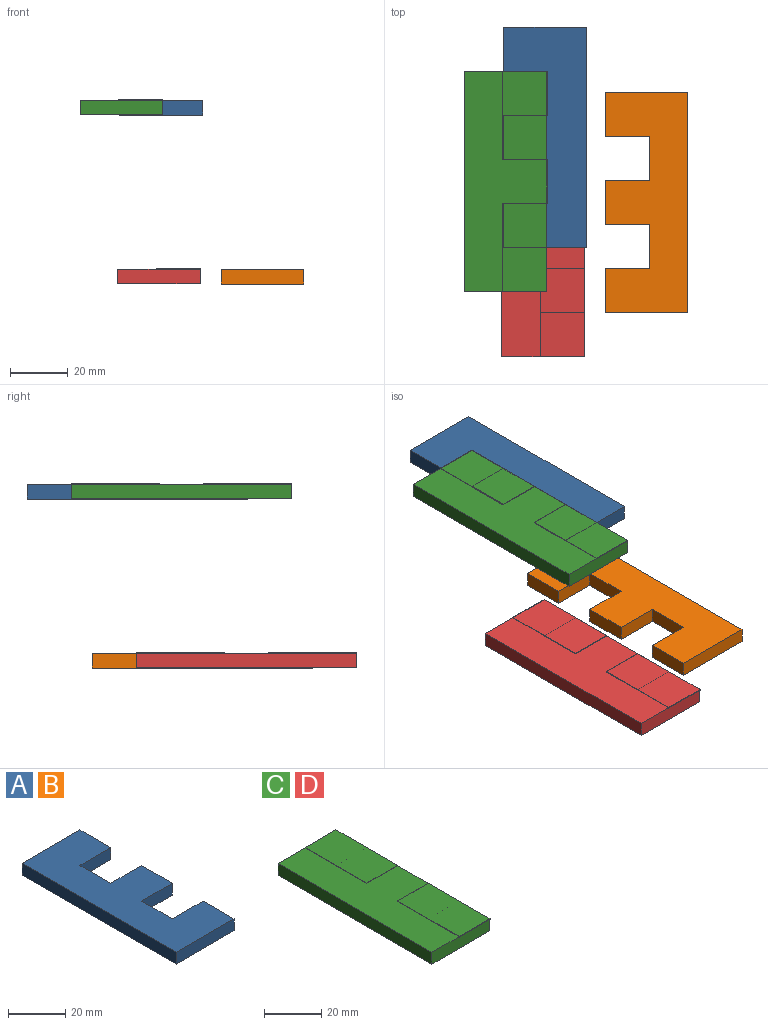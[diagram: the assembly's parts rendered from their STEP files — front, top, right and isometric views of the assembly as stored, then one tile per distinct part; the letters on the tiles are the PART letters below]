
ASSEMBLY  parts=4 mates=2
PART A: 14 faces, bbox 28.6x76.2x5.1 mm
  f0: plane 76.2x5.08mm, normal (-1,0,0), area 387.1mm2, adj f1,f11,f12,f13
  f1: plane 28.64x5.08mm, normal (0,-1,0), area 145.5mm2, adj f0,f2,f12,f13
  f2: plane 15.24x5.08mm, normal (1,0,0), area 77.4mm2, adj f1,f3,f12,f13
  f3: plane 15.24x5.08mm, normal (0,1,0), area 77.4mm2, adj f2,f4,f12,f13
  f4: plane 15.24x5.08mm, normal (1,0,0), area 77.4mm2, adj f3,f5,f12,f13
  f5: plane 15.24x5.08mm, normal (0,-1,0), area 77.4mm2, adj f4,f6,f12,f13
  f6: plane 15.24x5.08mm, normal (1,0,0), area 77.4mm2, adj f5,f7,f12,f13
  f7: plane 15.24x5.08mm, normal (0,1,0), area 77.4mm2, adj f6,f8,f12,f13
  f8: plane 15.24x5.08mm, normal (1,0,0), area 77.4mm2, adj f7,f9,f12,f13
  f9: plane 15.24x5.08mm, normal (0,-1,0), area 77.4mm2, adj f8,f10,f12,f13
  f10: plane 15.24x5.08mm, normal (1,0,0), area 77.4mm2, adj f9,f11,f12,f13
  f11: plane 28.64x5.08mm, normal (0,1,0), area 145.5mm2, adj f0,f10,f12,f13
  f12: plane 76.2x28.64mm, normal (0,0,1), area 1718.2mm2, adj f0,f1,f2,f3,f4,f5,f6,f7
  f13: plane 76.2x28.64mm, normal (0,0,-1), area 1718.2mm2, adj f0,f1,f2,f3,f4,f5,f6,f7
PART B: same geometry as A
PART C: 24 faces, bbox 28.6x76.3x5.2 mm
  f0: plane 15.24x5.08mm, normal (1,0,0), area 75.5mm2, adj f1,f7,f11,f12,f18,f20
  f1: plane 15.24x4.95mm, normal (0,1,0), area 75.5mm2, adj f0,f6,f11,f18
  f2: plane 15.24x4.95mm, normal (0,1,0), area 75.5mm2, adj f8,f9,f11,f13
  f3: plane 15.24x4.95mm, normal (0,-1,0), area 75.5mm2, adj f8,f9,f11,f13
  f4: plane 76.2x5.08mm, normal (-1,0,0), area 387.1mm2, adj f5,f10,f11,f12
  f5: plane 28.64x5.08mm, normal (0,-1,0), area 143.6mm2, adj f4,f6,f11,f12,f21,f22
  f6: plane 30.48x5.21mm, normal (1,0,0), area 83.2mm2, adj f1,f5,f11,f18,f19,f20,f22,f23
  f7: plane 15.24x5.08mm, normal (0,-1,0), area 77.4mm2, adj f0,f9,f11,f12
  f8: plane 15.24x4.95mm, normal (1,0,0), area 75.5mm2, adj f2,f3,f11,f13
  f9: plane 45.72x5.21mm, normal (1,0,0), area 160.6mm2, adj f2,f3,f7,f10,f11,f12,f13,f14
  f10: plane 28.64x5.08mm, normal (0,1,0), area 145.5mm2, adj f4,f9,f11,f12
  f11: plane 76.2x28.64mm, normal (0,0,-1), area 1718.2mm2, adj f0,f1,f2,f3,f4,f5,f6,f7
  f12: plane 76.2x28.64mm, normal (0,0,1), area 1253.7mm2, adj f0,f4,f5,f7,f9,f10,f14,f15
  f13: plane 15.24x15.24mm, normal (0,0,-1), area 232.3mm2, adj f2,f3,f8,f9
  f14: plane 15.24x0.13mm, normal (0,-1,0), area 1.9mm2, adj f9,f12,f16,f17
  f15: plane 15.24x0.13mm, normal (0,1,0), area 1.9mm2, adj f9,f12,f16,f17
  f16: plane 30.48x0.13mm, normal (-1,0,0), area 3.9mm2, adj f12,f14,f15,f17
  f17: plane 30.48x15.24mm, normal (0,0,1), area 464.5mm2, adj f9,f14,f15,f16
  f18: plane 15.24x15.15mm, normal (0,0,-1), area 230.9mm2, adj f0,f1,f6,f20
  f19: plane 15.24x0.25mm, normal (0,-1,0), area 3.9mm2, adj f6,f21,f22,f23
  f20: plane 15.24x0.25mm, normal (0,1,0), area 3.9mm2, adj f0,f6,f18,f21,f23
  f21: plane 30.48x0.25mm, normal (-1,0,0), area 3.9mm2, adj f5,f12,f19,f20,f22,f23
  f22: plane 15.24x0.09mm, normal (0,0,-1), area 1.4mm2, adj f5,f6,f19,f21
  f23: plane 30.48x15.24mm, normal (0,0,1), area 464.5mm2, adj f6,f19,f20,f21
PART D: same geometry as C
PLACE A rot(axis=(0,1,0),180deg) t=(-12.04,41.38,-34.12)mm
PLACE B rot(axis=(0,1,0),180deg) t=(23.01,18.95,-92.53)mm
PLACE C t=(2.92,26.14,-31.52)mm
PLACE D t=(15.81,3.71,-89.93)mm
MATE slider B.f2 <-> D.f0  axis (-1,0,0) through (23.01,-3.82,-92.53)mm
MATE slider A.f2 <-> C.f0  axis (-1,0,0) through (-12.04,18.61,-34.12)mm
